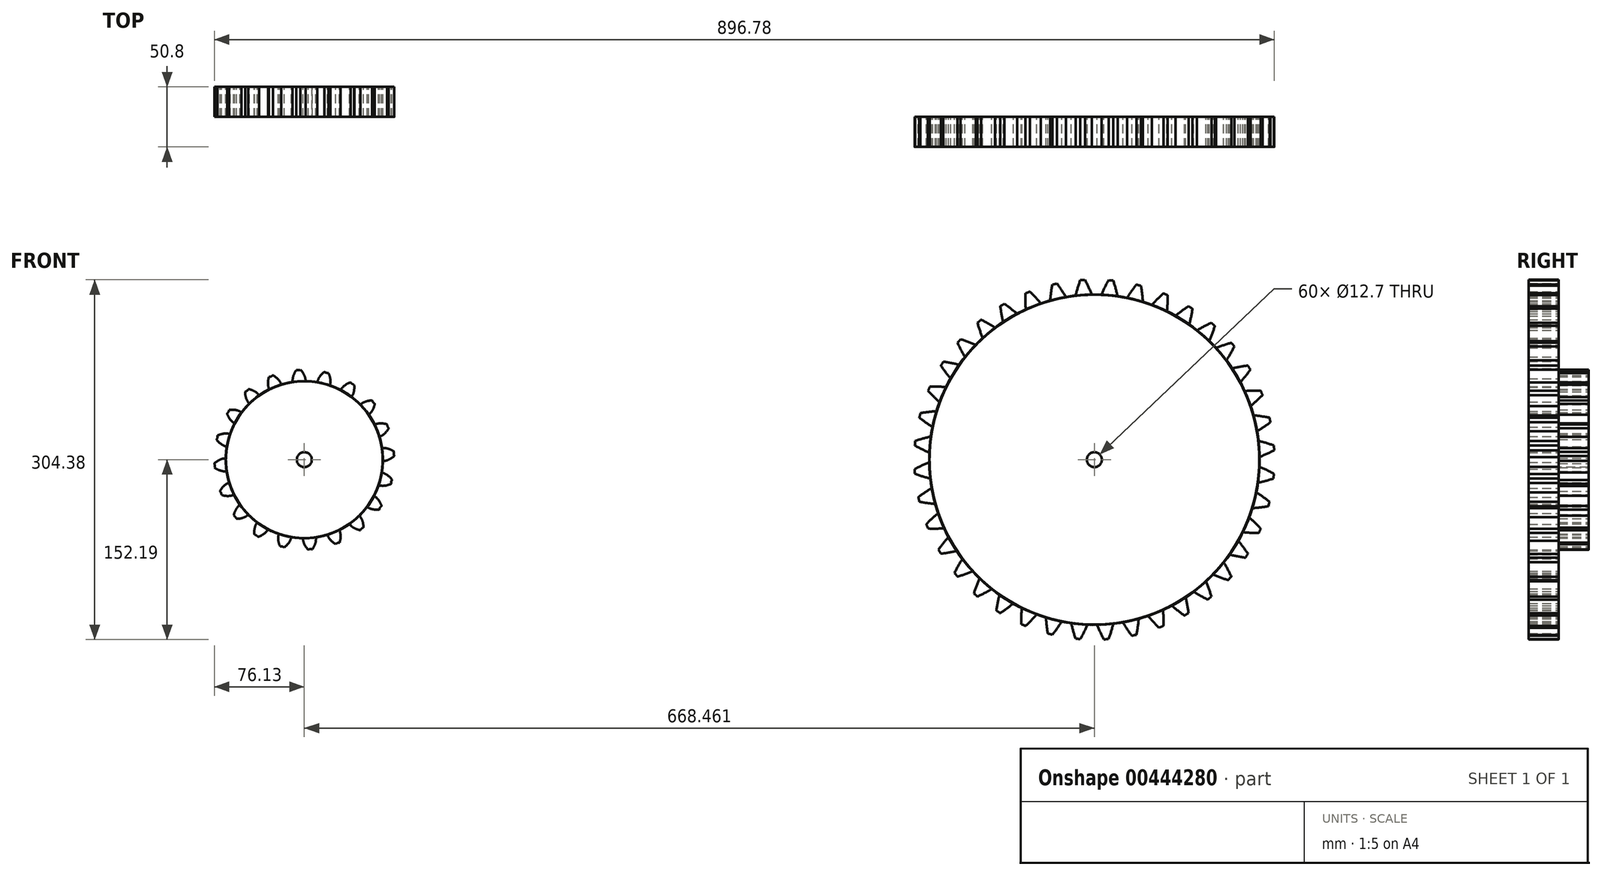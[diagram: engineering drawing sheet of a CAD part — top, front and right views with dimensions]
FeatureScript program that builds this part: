
annotation { "Feature Type Name" : "Feature", "Feature Type Description" : "" }
export const myFeature = defineFeature(function(context is Context, id is Id, definition is map)
    precondition{}
    {
        {
            var Q0;
            Q0=qCreatedBy(makeId("Front.planeOp"),FACE);
            var sketch = newSketch(context, id + "F0", { "sketchPlane" : qUnion([Q0])});
            skCircle(sketch, "E0", {"center": v(0, 0) * mm, "radius": 66.42 * mm});
            skCircle(sketch, "E1", {"center": v(0, 0) * mm, "radius": 71.37 * mm, "construction": true});
            skCircle(sketch, "E2", {"center": v(0, 0) * mm, "radius": 76.2 * mm, "construction": true});
            skLineSegment(sketch, "E3", {"start": v(0, 0) * mm, "end": v(0, 122.77) * mm, "construction": true});
            skLineSegment(sketch, "E4", {"start": v(0, 0) * mm, "end": v(-7.95, 121.32) * mm, "construction": true});
            skLineSegment(sketch, "E5", {"start": v(7.31, 71) * mm, "end": v(0, 71.37) * mm, "construction": true});
            skLineSegment(sketch, "E6", {"start": v(0, 71.37) * mm, "end": v(-108.9, 71.37) * mm, "construction": true});
            skLineSegment(sketch, "E7", {"start": v(0, 71.37) * mm, "end": v(-103.72, 33.62) * mm, "construction": true});
            skCircle(sketch, "E8", {"center": v(0, 0) * mm, "radius": 67.07 * mm, "construction": true});
            skCircle(sketch, "E9", {"center": v(0, 71.37) * mm, "radius": 14.6 * mm, "construction": true});
            skCircle(sketch, "E10", {"center": v(-13.46, 65.7) * mm, "radius": 14.6 * mm, "construction": true});
            skArc(sketch, "E11", {"start": v(0, 71.37) * mm, "mid": v(-1.41, 73.9) * mm, "end": v(-3.23, 76.13) * mm});
            skArc(sketch, "E12", {"start": v(1.13, 66.41) * mm, "mid": v(0.82, 68.95) * mm, "end": v(0, 71.37) * mm});
            skArc(sketch, "E13.MirrorCS", {"start": v(-9.32, 70.76) * mm, "mid": v(-8.24, 73.44) * mm, "end": v(-6.73, 75.9) * mm});
            skArc(sketch, "E14.MirrorCS", {"start": v(-9.79, 65.7) * mm, "mid": v(-9.8, 68.25) * mm, "end": v(-9.32, 70.76) * mm});
            skArc(sketch, "E15", {"start": v(-6.73, 75.9) * mm, "mid": v(-4.96, 75.67) * mm, "end": v(-3.23, 76.13) * mm});
            skSolve(sketch);
        }
        {
            var Q0;
            {var subQ0=sQuery(id+"F0.wireOp",EDGE,"E0");var subQ1=makeQuery(id+"F0.imprint","INTERSECT",VERTEX,{"derivedFrom":[subQ0,sQuery(id+"F0.wireOp",EDGE,"E12")]});Q0=makeQuery(id+"F0.imprint","IMPRINT",FACE,{"disambiguationData":[TD([[makeQuery(id+"F0.imprint","IMPRINT",EDGE,{"disambiguationData":[TD([[subQ1,-1.0]])],"derivedFrom":subQ0}),1.0]])]});}
            var Q1;
            Q1=makeQuery(id+"F0.imprint","IMPRINT",FACE,{"disambiguationData":[TD([[makeQuery(id+"F0.imprint","IMPRINT",EDGE,{"derivedFrom":sQuery(id+"F0.wireOp",EDGE,"E11")}),1.0]])]});
            extrude(context, id + "F1", {"entities" : qUnion([Q0, Q1]), "depth" : 25.4 * mm});
        }
        {
            var Q0;
            Q0=makeQuery(id+"F1.opExtrude","SWEPT_BODY",BODY,{"disambiguationData":[OSD([sQuery(id+"F0.wireOp",EDGE,"E0"),sQuery(id+"F0.wireOp",EDGE,"E11"),sQuery(id+"F0.wireOp",EDGE,"E12"),sQuery(id+"F0.wireOp",EDGE,"E13.MirrorCS"),sQuery(id+"F0.wireOp",EDGE,"E14.MirrorCS"),sQuery(id+"F0.wireOp",EDGE,"E15")])]});
            var Q1;
            Q1=makeQuery(id+"F1.opExtrude","SWEPT_FACE",FACE,{"disambiguationData":[OSD([sQuery(id+"F0.wireOp",EDGE,"E0")])]});
            circularPattern(context, id + "F2", {"entities" : qUnion([Q0]), "axis" : qUnion([Q1]), "angle" : 360 * degree, "instanceCount" : 20, "equalSpace" : true});
        }
        {
            var Q0;
            Q0=makeQuery(id+"F1.opExtrude","CAP_FACE",FACE,{"disambiguationData":[OSD([sQuery(id+"F0.wireOp",EDGE,"E0"),sQuery(id+"F0.wireOp",EDGE,"E11"),sQuery(id+"F0.wireOp",EDGE,"E12"),sQuery(id+"F0.wireOp",EDGE,"E13.MirrorCS"),sQuery(id+"F0.wireOp",EDGE,"E14.MirrorCS"),sQuery(id+"F0.wireOp",EDGE,"E15")])],"isStart":false});
            var sketch = newSketch(context, id + "F3", { "sketchPlane" : qUnion([Q0])});
            skCircle(sketch, "E16", {"center": v(0, 0) * mm, "radius": 6.35 * mm});
            skSolve(sketch);
        }
        {
            var Q0;
            Q0=sQuery(id+"F3.wireOp",VERTEX,"E16.center");
            var Q1;
            Q1=makeQuery(id+"F1.opExtrude","SWEPT_BODY",BODY,{"disambiguationData":[OSD([sQuery(id+"F0.wireOp",EDGE,"E0"),sQuery(id+"F0.wireOp",EDGE,"E11"),sQuery(id+"F0.wireOp",EDGE,"E12"),sQuery(id+"F0.wireOp",EDGE,"E13.MirrorCS"),sQuery(id+"F0.wireOp",EDGE,"E14.MirrorCS"),sQuery(id+"F0.wireOp",EDGE,"E15")])]});
            var Q2;
            Q2=makeQuery(id+"F2.opPattern","COPY",BODY,{"derivedFrom":makeQuery(id+"F1.opExtrude","SWEPT_BODY",BODY,{"disambiguationData":[OSD([sQuery(id+"F0.wireOp",EDGE,"E0"),sQuery(id+"F0.wireOp",EDGE,"E11"),sQuery(id+"F0.wireOp",EDGE,"E12"),sQuery(id+"F0.wireOp",EDGE,"E13.MirrorCS"),sQuery(id+"F0.wireOp",EDGE,"E14.MirrorCS"),sQuery(id+"F0.wireOp",EDGE,"E15")])]}),"instanceName":"1"});
            var Q3;
            Q3=makeQuery(id+"F2.opPattern","COPY",BODY,{"derivedFrom":makeQuery(id+"F1.opExtrude","SWEPT_BODY",BODY,{"disambiguationData":[OSD([sQuery(id+"F0.wireOp",EDGE,"E0"),sQuery(id+"F0.wireOp",EDGE,"E11"),sQuery(id+"F0.wireOp",EDGE,"E12"),sQuery(id+"F0.wireOp",EDGE,"E13.MirrorCS"),sQuery(id+"F0.wireOp",EDGE,"E14.MirrorCS"),sQuery(id+"F0.wireOp",EDGE,"E15")])]}),"instanceName":"2"});
            var Q4;
            Q4=makeQuery(id+"F2.opPattern","COPY",BODY,{"derivedFrom":makeQuery(id+"F1.opExtrude","SWEPT_BODY",BODY,{"disambiguationData":[OSD([sQuery(id+"F0.wireOp",EDGE,"E0"),sQuery(id+"F0.wireOp",EDGE,"E11"),sQuery(id+"F0.wireOp",EDGE,"E12"),sQuery(id+"F0.wireOp",EDGE,"E13.MirrorCS"),sQuery(id+"F0.wireOp",EDGE,"E14.MirrorCS"),sQuery(id+"F0.wireOp",EDGE,"E15")])]}),"instanceName":"3"});
            var Q5;
            Q5=makeQuery(id+"F2.opPattern","COPY",BODY,{"derivedFrom":makeQuery(id+"F1.opExtrude","SWEPT_BODY",BODY,{"disambiguationData":[OSD([sQuery(id+"F0.wireOp",EDGE,"E0"),sQuery(id+"F0.wireOp",EDGE,"E11"),sQuery(id+"F0.wireOp",EDGE,"E12"),sQuery(id+"F0.wireOp",EDGE,"E13.MirrorCS"),sQuery(id+"F0.wireOp",EDGE,"E14.MirrorCS"),sQuery(id+"F0.wireOp",EDGE,"E15")])]}),"instanceName":"4"});
            var Q6;
            Q6=makeQuery(id+"F2.opPattern","COPY",BODY,{"derivedFrom":makeQuery(id+"F1.opExtrude","SWEPT_BODY",BODY,{"disambiguationData":[OSD([sQuery(id+"F0.wireOp",EDGE,"E0"),sQuery(id+"F0.wireOp",EDGE,"E11"),sQuery(id+"F0.wireOp",EDGE,"E12"),sQuery(id+"F0.wireOp",EDGE,"E13.MirrorCS"),sQuery(id+"F0.wireOp",EDGE,"E14.MirrorCS"),sQuery(id+"F0.wireOp",EDGE,"E15")])]}),"instanceName":"5"});
            var Q7;
            Q7=makeQuery(id+"F2.opPattern","COPY",BODY,{"derivedFrom":makeQuery(id+"F1.opExtrude","SWEPT_BODY",BODY,{"disambiguationData":[OSD([sQuery(id+"F0.wireOp",EDGE,"E0"),sQuery(id+"F0.wireOp",EDGE,"E11"),sQuery(id+"F0.wireOp",EDGE,"E12"),sQuery(id+"F0.wireOp",EDGE,"E13.MirrorCS"),sQuery(id+"F0.wireOp",EDGE,"E14.MirrorCS"),sQuery(id+"F0.wireOp",EDGE,"E15")])]}),"instanceName":"6"});
            var Q8;
            Q8=makeQuery(id+"F2.opPattern","COPY",BODY,{"derivedFrom":makeQuery(id+"F1.opExtrude","SWEPT_BODY",BODY,{"disambiguationData":[OSD([sQuery(id+"F0.wireOp",EDGE,"E0"),sQuery(id+"F0.wireOp",EDGE,"E11"),sQuery(id+"F0.wireOp",EDGE,"E12"),sQuery(id+"F0.wireOp",EDGE,"E13.MirrorCS"),sQuery(id+"F0.wireOp",EDGE,"E14.MirrorCS"),sQuery(id+"F0.wireOp",EDGE,"E15")])]}),"instanceName":"7"});
            var Q9;
            Q9=makeQuery(id+"F2.opPattern","COPY",BODY,{"derivedFrom":makeQuery(id+"F1.opExtrude","SWEPT_BODY",BODY,{"disambiguationData":[OSD([sQuery(id+"F0.wireOp",EDGE,"E0"),sQuery(id+"F0.wireOp",EDGE,"E11"),sQuery(id+"F0.wireOp",EDGE,"E12"),sQuery(id+"F0.wireOp",EDGE,"E13.MirrorCS"),sQuery(id+"F0.wireOp",EDGE,"E14.MirrorCS"),sQuery(id+"F0.wireOp",EDGE,"E15")])]}),"instanceName":"8"});
            var Q10;
            Q10=makeQuery(id+"F2.opPattern","COPY",BODY,{"derivedFrom":makeQuery(id+"F1.opExtrude","SWEPT_BODY",BODY,{"disambiguationData":[OSD([sQuery(id+"F0.wireOp",EDGE,"E0"),sQuery(id+"F0.wireOp",EDGE,"E11"),sQuery(id+"F0.wireOp",EDGE,"E12"),sQuery(id+"F0.wireOp",EDGE,"E13.MirrorCS"),sQuery(id+"F0.wireOp",EDGE,"E14.MirrorCS"),sQuery(id+"F0.wireOp",EDGE,"E15")])]}),"instanceName":"9"});
            var Q11;
            Q11=makeQuery(id+"F2.opPattern","COPY",BODY,{"derivedFrom":makeQuery(id+"F1.opExtrude","SWEPT_BODY",BODY,{"disambiguationData":[OSD([sQuery(id+"F0.wireOp",EDGE,"E0"),sQuery(id+"F0.wireOp",EDGE,"E11"),sQuery(id+"F0.wireOp",EDGE,"E12"),sQuery(id+"F0.wireOp",EDGE,"E13.MirrorCS"),sQuery(id+"F0.wireOp",EDGE,"E14.MirrorCS"),sQuery(id+"F0.wireOp",EDGE,"E15")])]}),"instanceName":"10"});
            var Q12;
            Q12=makeQuery(id+"F2.opPattern","COPY",BODY,{"derivedFrom":makeQuery(id+"F1.opExtrude","SWEPT_BODY",BODY,{"disambiguationData":[OSD([sQuery(id+"F0.wireOp",EDGE,"E0"),sQuery(id+"F0.wireOp",EDGE,"E11"),sQuery(id+"F0.wireOp",EDGE,"E12"),sQuery(id+"F0.wireOp",EDGE,"E13.MirrorCS"),sQuery(id+"F0.wireOp",EDGE,"E14.MirrorCS"),sQuery(id+"F0.wireOp",EDGE,"E15")])]}),"instanceName":"11"});
            var Q13;
            Q13=makeQuery(id+"F2.opPattern","COPY",BODY,{"derivedFrom":makeQuery(id+"F1.opExtrude","SWEPT_BODY",BODY,{"disambiguationData":[OSD([sQuery(id+"F0.wireOp",EDGE,"E0"),sQuery(id+"F0.wireOp",EDGE,"E11"),sQuery(id+"F0.wireOp",EDGE,"E12"),sQuery(id+"F0.wireOp",EDGE,"E13.MirrorCS"),sQuery(id+"F0.wireOp",EDGE,"E14.MirrorCS"),sQuery(id+"F0.wireOp",EDGE,"E15")])]}),"instanceName":"12"});
            var Q14;
            Q14=makeQuery(id+"F2.opPattern","COPY",BODY,{"derivedFrom":makeQuery(id+"F1.opExtrude","SWEPT_BODY",BODY,{"disambiguationData":[OSD([sQuery(id+"F0.wireOp",EDGE,"E0"),sQuery(id+"F0.wireOp",EDGE,"E11"),sQuery(id+"F0.wireOp",EDGE,"E12"),sQuery(id+"F0.wireOp",EDGE,"E13.MirrorCS"),sQuery(id+"F0.wireOp",EDGE,"E14.MirrorCS"),sQuery(id+"F0.wireOp",EDGE,"E15")])]}),"instanceName":"13"});
            var Q15;
            Q15=makeQuery(id+"F2.opPattern","COPY",BODY,{"derivedFrom":makeQuery(id+"F1.opExtrude","SWEPT_BODY",BODY,{"disambiguationData":[OSD([sQuery(id+"F0.wireOp",EDGE,"E0"),sQuery(id+"F0.wireOp",EDGE,"E11"),sQuery(id+"F0.wireOp",EDGE,"E12"),sQuery(id+"F0.wireOp",EDGE,"E13.MirrorCS"),sQuery(id+"F0.wireOp",EDGE,"E14.MirrorCS"),sQuery(id+"F0.wireOp",EDGE,"E15")])]}),"instanceName":"14"});
            var Q16;
            Q16=makeQuery(id+"F2.opPattern","COPY",BODY,{"derivedFrom":makeQuery(id+"F1.opExtrude","SWEPT_BODY",BODY,{"disambiguationData":[OSD([sQuery(id+"F0.wireOp",EDGE,"E0"),sQuery(id+"F0.wireOp",EDGE,"E11"),sQuery(id+"F0.wireOp",EDGE,"E12"),sQuery(id+"F0.wireOp",EDGE,"E13.MirrorCS"),sQuery(id+"F0.wireOp",EDGE,"E14.MirrorCS"),sQuery(id+"F0.wireOp",EDGE,"E15")])]}),"instanceName":"15"});
            var Q17;
            Q17=makeQuery(id+"F2.opPattern","COPY",BODY,{"derivedFrom":makeQuery(id+"F1.opExtrude","SWEPT_BODY",BODY,{"disambiguationData":[OSD([sQuery(id+"F0.wireOp",EDGE,"E0"),sQuery(id+"F0.wireOp",EDGE,"E11"),sQuery(id+"F0.wireOp",EDGE,"E12"),sQuery(id+"F0.wireOp",EDGE,"E13.MirrorCS"),sQuery(id+"F0.wireOp",EDGE,"E14.MirrorCS"),sQuery(id+"F0.wireOp",EDGE,"E15")])]}),"instanceName":"16"});
            var Q18;
            Q18=makeQuery(id+"F2.opPattern","COPY",BODY,{"derivedFrom":makeQuery(id+"F1.opExtrude","SWEPT_BODY",BODY,{"disambiguationData":[OSD([sQuery(id+"F0.wireOp",EDGE,"E0"),sQuery(id+"F0.wireOp",EDGE,"E11"),sQuery(id+"F0.wireOp",EDGE,"E12"),sQuery(id+"F0.wireOp",EDGE,"E13.MirrorCS"),sQuery(id+"F0.wireOp",EDGE,"E14.MirrorCS"),sQuery(id+"F0.wireOp",EDGE,"E15")])]}),"instanceName":"17"});
            var Q19;
            Q19=makeQuery(id+"F2.opPattern","COPY",BODY,{"derivedFrom":makeQuery(id+"F1.opExtrude","SWEPT_BODY",BODY,{"disambiguationData":[OSD([sQuery(id+"F0.wireOp",EDGE,"E0"),sQuery(id+"F0.wireOp",EDGE,"E11"),sQuery(id+"F0.wireOp",EDGE,"E12"),sQuery(id+"F0.wireOp",EDGE,"E13.MirrorCS"),sQuery(id+"F0.wireOp",EDGE,"E14.MirrorCS"),sQuery(id+"F0.wireOp",EDGE,"E15")])]}),"instanceName":"18"});
            var Q20;
            Q20=makeQuery(id+"F2.opPattern","COPY",BODY,{"derivedFrom":makeQuery(id+"F1.opExtrude","SWEPT_BODY",BODY,{"disambiguationData":[OSD([sQuery(id+"F0.wireOp",EDGE,"E0"),sQuery(id+"F0.wireOp",EDGE,"E11"),sQuery(id+"F0.wireOp",EDGE,"E12"),sQuery(id+"F0.wireOp",EDGE,"E13.MirrorCS"),sQuery(id+"F0.wireOp",EDGE,"E14.MirrorCS"),sQuery(id+"F0.wireOp",EDGE,"E15")])]}),"instanceName":"19"});
            hole(context, id + "F4", {"style" : HoleStyle.SIMPLE, "endStyle" : HoleEndStyle.THROUGH, "holeDiameter" : 12.7 * mm, "isTappedThrough" : true, "tappedDepth" : 12.7 * mm, "tapClearance" : 3, "locations" : qUnion([Q0]), "scope" : qUnion([Q1, Q2, Q3, Q4, Q5, Q6, Q7, Q8, Q9, Q10, Q11, Q12, Q13, Q14, Q15, Q16, Q17, Q18, Q19, Q20])});
        }
        {
            var Q0;
            Q0=makeQuery(id+"F2.opPattern","COPY",FACE,{"derivedFrom":makeQuery(id+"F1.opExtrude","CAP_FACE",FACE,{"disambiguationData":[OSD([sQuery(id+"F0.wireOp",EDGE,"E0"),sQuery(id+"F0.wireOp",EDGE,"E11"),sQuery(id+"F0.wireOp",EDGE,"E12"),sQuery(id+"F0.wireOp",EDGE,"E13.MirrorCS"),sQuery(id+"F0.wireOp",EDGE,"E14.MirrorCS"),sQuery(id+"F0.wireOp",EDGE,"E15")])],"isStart":false}),"instanceName":"10"});
            var sketch = newSketch(context, id + "F5", { "sketchPlane" : qUnion([Q0])});
            skCircle(sketch, "E17", {"center": v(668.46, 0) * mm, "radius": 139.7 * mm});
            skCircle(sketch, "E18", {"center": v(668.46, 0) * mm, "radius": 145.8 * mm, "construction": true});
            skCircle(sketch, "E19", {"center": v(668.46, 0) * mm, "radius": 152.4 * mm, "construction": true});
            skLineSegment(sketch, "E20", {"start": v(668.46, 0) * mm, "end": v(668.46, 228.67) * mm, "construction": true});
            skLineSegment(sketch, "E21", {"start": v(668.46, 145.8) * mm, "end": v(420.16, 145.8) * mm, "construction": true});
            skLineSegment(sketch, "E22", {"start": v(668.46, 145.8) * mm, "end": v(524.78, 93.5) * mm, "construction": true});
            skCircle(sketch, "E23", {"center": v(668.46, 0) * mm, "radius": 137 * mm, "construction": true});
            skCircle(sketch, "E24", {"center": v(668.46, 145.8) * mm, "radius": 7.3 * mm, "construction": true});
            skLineSegment(sketch, "E25", {"start": v(668.46, 0) * mm, "end": v(653.6, 226.69) * mm, "construction": true});
            skCircle(sketch, "E26", {"center": v(659.5, 136.71) * mm, "radius": 7.3 * mm, "construction": true});
            skArc(sketch, "E27", {"start": v(666.17, 139.68) * mm, "mid": v(663.5, 146.02) * mm, "end": v(660.44, 152.19) * mm});
            skArc(sketch, "E28.MirrorCS", {"start": v(652.5, 138.79) * mm, "mid": v(654.33, 145.42) * mm, "end": v(656.55, 151.93) * mm});
            skArc(sketch, "E29", {"start": v(656.55, 151.93) * mm, "mid": v(658.5, 151.96) * mm, "end": v(660.44, 152.19) * mm});
            skCircle(sketch, "E30", {"center": v(668.46, 0) * mm, "radius": 6.35 * mm});
            skSolve(sketch);
        }
        {
            var Q0;
            {var subQ0=sQuery(id+"F5.wireOp",EDGE,"E27");Q0=makeQuery(id+"F5.imprint","IMPRINT",FACE,{"disambiguationData":[TD([[makeQuery(id+"F5.imprint","IMPRINT",EDGE,{"derivedFrom":subQ0}),1.0]])]});}
            var Q1;
            {var subQ0=sQuery(id+"F5.wireOp",EDGE,"E17");var subQ1=makeQuery(id+"F5.imprint","INTERSECT",VERTEX,{"derivedFrom":[subQ0,sQuery(id+"F5.wireOp",EDGE,"E27")]});Q1=makeQuery(id+"F5.imprint","IMPRINT",FACE,{"disambiguationData":[TD([[makeQuery(id+"F5.imprint","IMPRINT",EDGE,{"disambiguationData":[TD([[subQ1,-1.0]])],"derivedFrom":subQ0}),1.0]])]});}
            extrude(context, id + "F6", {"entities" : qUnion([Q0, Q1]), "depth" : 25.4 * mm});
        }
        {
            var Q0;
            Q0=makeQuery(id+"F6.opExtrude","SWEPT_BODY",BODY,{"disambiguationData":[OSD([sQuery(id+"F5.wireOp",EDGE,"E17"),sQuery(id+"F5.wireOp",EDGE,"E27"),sQuery(id+"F5.wireOp",EDGE,"E28.MirrorCS"),sQuery(id+"F5.wireOp",EDGE,"E29")])]});
            var Q1;
            Q1=makeQuery(id+"F6.opExtrude","SWEPT_FACE",FACE,{"disambiguationData":[OSD([sQuery(id+"F5.wireOp",EDGE,"E17")])]});
            circularPattern(context, id + "F7", {"entities" : qUnion([Q0]), "axis" : qUnion([Q1]), "angle" : 360 * degree, "instanceCount" : 40, "equalSpace" : true});
        }
    });
